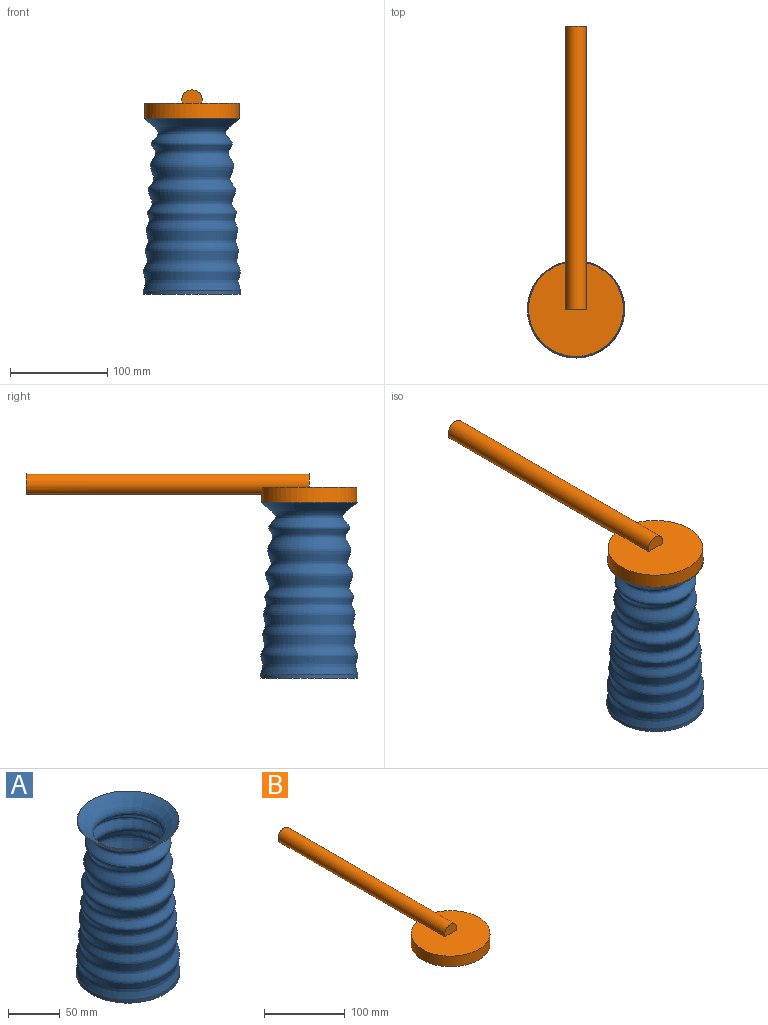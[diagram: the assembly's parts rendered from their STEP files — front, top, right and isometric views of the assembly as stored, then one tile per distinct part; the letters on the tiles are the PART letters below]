
ASSEMBLY  parts=2 mates=1
PART A: 6 faces, bbox 100x100x181.1 mm
  f0: cylinder r=50mm len=100mm, axis (0,0,-1), area 1256.6mm2, adj f1,f3
  f1: plane 100x100mm, normal (0,0,-1), area 7854mm2, adj f0
  f2: cone r=49.33mm half-angle=34.9deg, axis (0,0,-1), area 308.1mm2, adj f3,f4
  f3: revolved ~176.33x100mm, area 107019.1mm2, adj f0,f2
  f4: revolved ~177.15x97.88mm, area 104135mm2, adj f2,f5
  f5: plane 97.88x97.88mm, normal (0,0,1), area 7524.6mm2, adj f4
PART B: 12 faces, bbox 97.5x340x29.8 mm
  f0: cylinder r=48.76mm len=97.51mm, axis (0,0,-1), area 4771.4mm2, adj f1,f2,f3,f9
  f1: plane 97.51x96.5mm, normal (0,0,1), area 6511.8mm2, adj f0,f9,f11
  f2: plane 97.51x97.51mm, normal (0,0,-1), area 7468.2mm2, adj f0
  f3: cylinder r=2.95mm len=5.91mm, axis (0,-1,0), area 46.4mm2, adj f0,f4
  f4: cylinder r=46.26mm len=92.51mm, axis (0,0,-1), area 3113.8mm2, adj f3,f5,f6,f8
  f5: plane 92.51x91.7mm, normal (0,0,-1), area 5927.9mm2, adj f4,f7,f8
  f6: plane 92.51x92.51mm, normal (0,0,1), area 6722mm2, adj f4
  f7: plane 17.27x4.58mm, normal (0,-1,0), area 55.6mm2, adj f5,f8
  f8: cylinder r=10.43mm len=46.26mm, axis (0,-1,0), area 934.8mm2, adj f4,f5,f7
  f9: cylinder r=10.43mm len=291.2mm, axis (0,-1,0), area 17827mm2, adj f0,f1,f10,f11
  f10: plane 20.86x20.86mm, normal (0,1,0), area 341.7mm2, adj f9
  f11: plane 20.86x13.78mm, normal (0,-1,0), area 239.5mm2, adj f1,f9
PLACE A t=(-78.24,21.61,9.61)mm
PLACE B t=(-78.24,21.61,189.93)mm
MATE fastened B.f0 <-> A.f2  axis (0,0,-1) through (-78.24,21.61,189.93)mm
